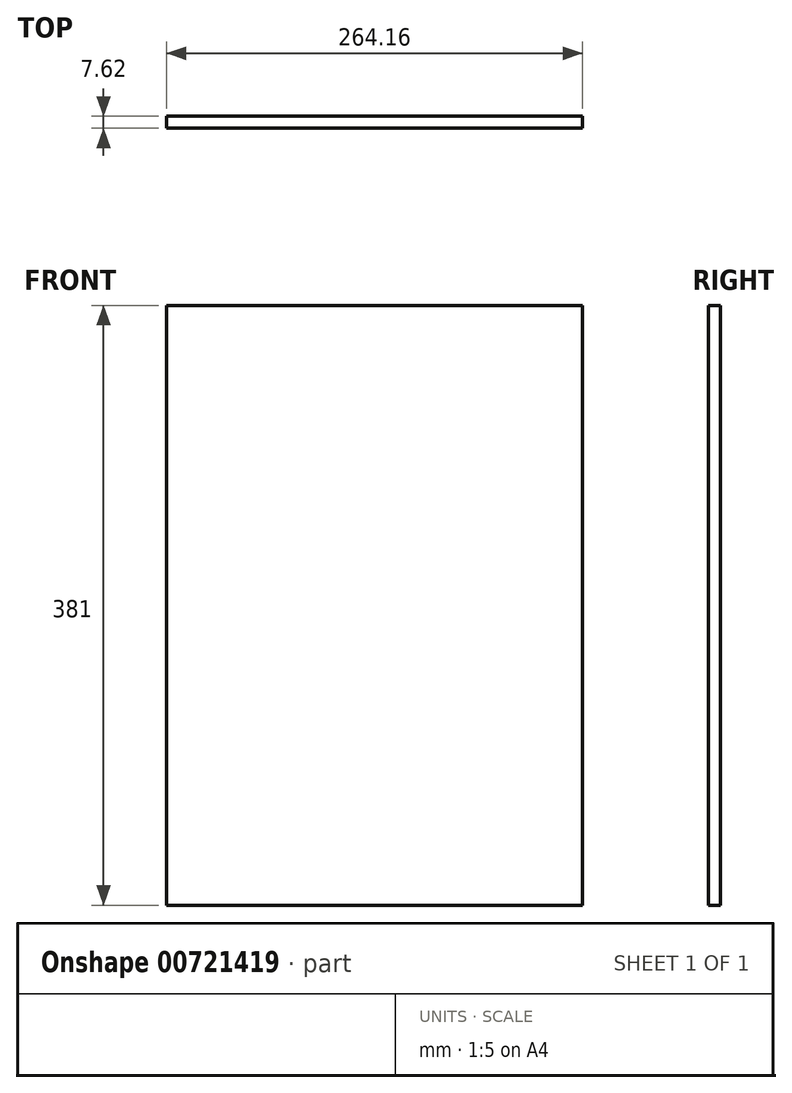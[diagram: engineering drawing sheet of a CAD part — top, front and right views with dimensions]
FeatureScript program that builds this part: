
annotation { "Feature Type Name" : "Feature", "Feature Type Description" : "" }
export const myFeature = defineFeature(function(context is Context, id is Id, definition is map)
    precondition{}
    {
        {
            var Q0;
            Q0=qCreatedBy(makeId("Front.planeOp"),FACE);
            var sketch = newSketch(context, id + "F0", { "sketchPlane" : qUnion([Q0])});
            skLineSegment(sketch, "E0.bottom", {"start": v(-135.3, 138.26) * mm, "end": v(128.87, 138.26) * mm});
            skLineSegment(sketch, "E0.top", {"start": v(-135.3, -242.74) * mm, "end": v(128.87, -242.74) * mm});
            skLineSegment(sketch, "E0.left", {"start": v(-135.3, 138.26) * mm, "end": v(-135.3, -242.74) * mm});
            skLineSegment(sketch, "E0.right", {"start": v(128.87, 138.26) * mm, "end": v(128.87, -242.74) * mm});
            skSolve(sketch);
        }
        {
            var Q0;
            Q0=makeQuery(id+"F0.imprint","IMPRINT",FACE,{"disambiguationData":[TD([[makeQuery(id+"F0.imprint","IMPRINT",EDGE,{"derivedFrom":sQuery(id+"F0.wireOp",EDGE,"E0.bottom")}),-1.0]])]});
            extrude(context, id + "F1", {"entities" : qUnion([Q0]), "depth" : 7.62 * mm, "offsetDistance" : 25.4 * mm});
        }
    });
